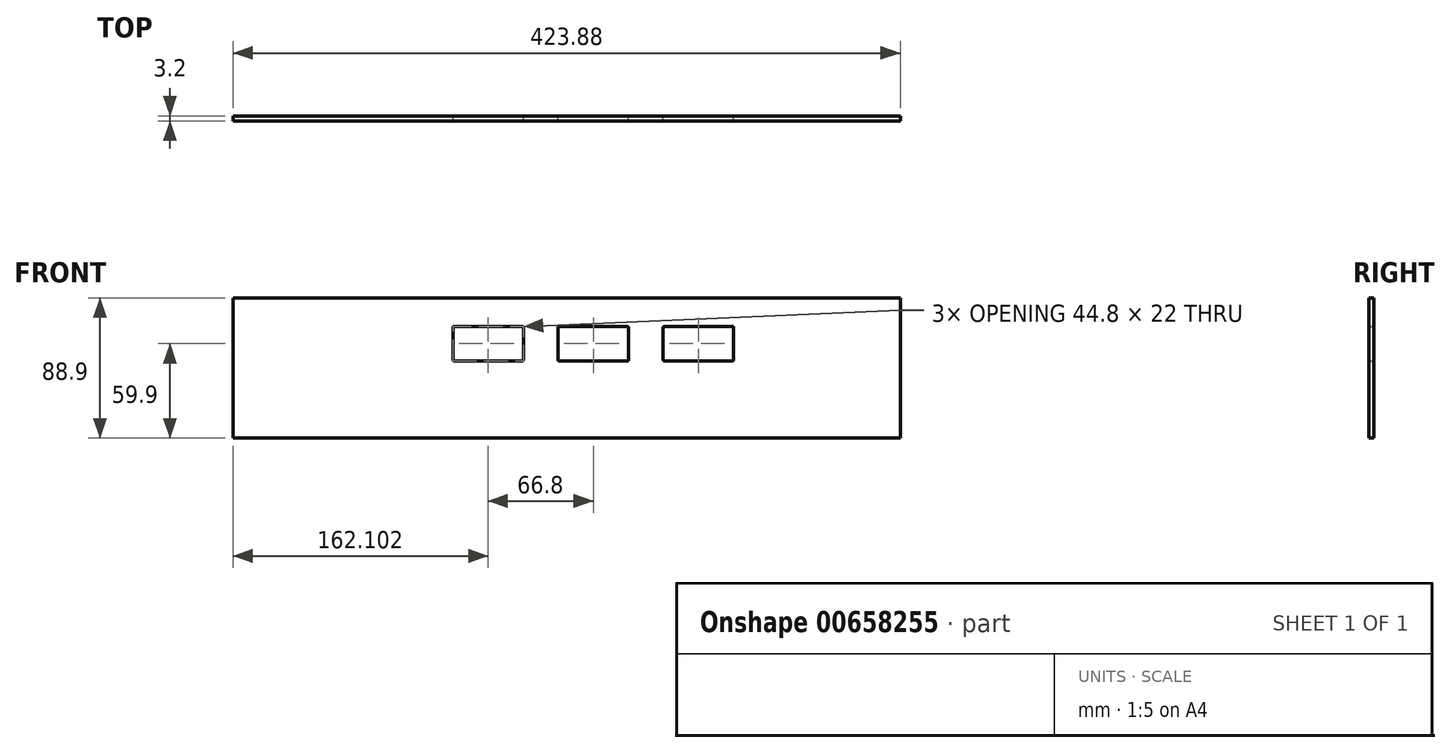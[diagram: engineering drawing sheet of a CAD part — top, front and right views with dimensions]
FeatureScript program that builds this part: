
annotation { "Feature Type Name" : "Feature", "Feature Type Description" : "" }
export const myFeature = defineFeature(function(context is Context, id is Id, definition is map)
    precondition{}
    {
        {
            var Q0;
            Q0=qCreatedBy(makeId("Front.planeOp"),FACE);
            var sketch = newSketch(context, id + "F0", { "sketchPlane" : qUnion([Q0])});
            skLineSegment(sketch, "E0.bottom", {"start": v(-211.94, 44.45) * mm, "end": v(211.94, 44.45) * mm});
            skLineSegment(sketch, "E0.top", {"start": v(-211.94, -44.45) * mm, "end": v(211.94, -44.45) * mm});
            skLineSegment(sketch, "E0.left", {"start": v(-211.94, 44.45) * mm, "end": v(-211.94, -44.45) * mm});
            skLineSegment(sketch, "E0.right", {"start": v(211.94, 44.45) * mm, "end": v(211.94, -44.45) * mm});
            skPoint(sketch, "E1", {"position": v(0, 44.45) * mm});
            skPoint(sketch, "E2", {"position": v(-211.94, 0) * mm});
            skLineSegment(sketch, "E3", {"start": v(-211.94, 34.93) * mm, "end": v(211.94, 34.93) * mm, "construction": true});
            skLineSegment(sketch, "E4", {"start": v(-211.94, -34.93) * mm, "end": v(211.94, -34.93) * mm, "construction": true});
            skLineSegment(sketch, "E5", {"start": v(-211.94, 34.93) * mm, "end": v(-211.94, -34.93) * mm, "construction": true});
            skLineSegment(sketch, "E6", {"start": v(-97.64, 34.93) * mm, "end": v(-97.64, -34.93) * mm, "construction": true});
            skLineSegment(sketch, "E7", {"start": v(-72.24, 34.93) * mm, "end": v(-72.24, -34.93) * mm, "construction": true});
            skLineSegment(sketch, "E8.bottom", {"start": v(-71.44, 26.45) * mm, "end": v(-28.23, 26.45) * mm});
            skLineSegment(sketch, "E8.top", {"start": v(-71.44, 4.45) * mm, "end": v(-28.23, 4.45) * mm});
            skLineSegment(sketch, "E8.left", {"start": v(-72.24, 25.66) * mm, "end": v(-72.24, 5.24) * mm});
            skLineSegment(sketch, "E8.right", {"start": v(-27.44, 25.66) * mm, "end": v(-27.44, 5.24) * mm});
            skLineSegment(sketch, "E9.bottom", {"start": v(-4.64, 26.45) * mm, "end": v(38.57, 26.45) * mm});
            skLineSegment(sketch, "E9.top", {"start": v(-4.64, 4.45) * mm, "end": v(38.57, 4.45) * mm});
            skLineSegment(sketch, "E9.left", {"start": v(-5.44, 25.66) * mm, "end": v(-5.44, 5.24) * mm});
            skLineSegment(sketch, "E9.right", {"start": v(39.36, 25.66) * mm, "end": v(39.36, 5.24) * mm});
            skLineSegment(sketch, "E10.bottom", {"start": v(62.16, 26.45) * mm, "end": v(105.37, 26.45) * mm});
            skLineSegment(sketch, "E10.top", {"start": v(62.16, 4.45) * mm, "end": v(105.37, 4.45) * mm});
            skLineSegment(sketch, "E10.left", {"start": v(61.36, 25.66) * mm, "end": v(61.36, 5.24) * mm});
            skLineSegment(sketch, "E10.right", {"start": v(106.16, 25.66) * mm, "end": v(106.16, 5.24) * mm});
            skPoint(sketch, "E11.visualSharp", {"position": v(-27.44, 26.45) * mm});
            skArc(sketch, "E11.filletArc", {"start": v(-27.44, 25.66) * mm, "mid": v(-27.67, 26.22) * mm, "end": v(-28.23, 26.45) * mm});
            skPoint(sketch, "E12.visualSharp", {"position": v(-27.44, 4.45) * mm});
            skArc(sketch, "E12.filletArc", {"start": v(-28.23, 4.45) * mm, "mid": v(-27.67, 4.68) * mm, "end": v(-27.44, 5.24) * mm});
            skPoint(sketch, "E13.visualSharp", {"position": v(-72.24, 4.45) * mm});
            skArc(sketch, "E13.filletArc", {"start": v(-72.24, 5.24) * mm, "mid": v(-72, 4.68) * mm, "end": v(-71.44, 4.45) * mm});
            skPoint(sketch, "E14.visualSharp", {"position": v(-72.24, 26.45) * mm});
            skArc(sketch, "E14.filletArc", {"start": v(-71.44, 26.45) * mm, "mid": v(-72, 26.22) * mm, "end": v(-72.24, 25.66) * mm});
            skPoint(sketch, "E15.visualSharp", {"position": v(-5.44, 26.45) * mm});
            skArc(sketch, "E15.filletArc", {"start": v(-4.64, 26.45) * mm, "mid": v(-5.2, 26.22) * mm, "end": v(-5.44, 25.66) * mm});
            skPoint(sketch, "E16.visualSharp", {"position": v(-5.44, 4.45) * mm});
            skArc(sketch, "E16.filletArc", {"start": v(-5.44, 5.24) * mm, "mid": v(-5.2, 4.68) * mm, "end": v(-4.64, 4.45) * mm});
            skPoint(sketch, "E17.visualSharp", {"position": v(39.36, 26.45) * mm});
            skArc(sketch, "E17.filletArc", {"start": v(39.36, 25.66) * mm, "mid": v(39.13, 26.22) * mm, "end": v(38.57, 26.45) * mm});
            skPoint(sketch, "E18.visualSharp", {"position": v(39.36, 4.45) * mm});
            skArc(sketch, "E18.filletArc", {"start": v(38.57, 4.45) * mm, "mid": v(39.13, 4.68) * mm, "end": v(39.36, 5.24) * mm});
            skPoint(sketch, "E19.visualSharp", {"position": v(61.36, 26.45) * mm});
            skArc(sketch, "E19.filletArc", {"start": v(62.16, 26.45) * mm, "mid": v(61.6, 26.22) * mm, "end": v(61.36, 25.66) * mm});
            skPoint(sketch, "E20.visualSharp", {"position": v(61.36, 4.45) * mm});
            skArc(sketch, "E20.filletArc", {"start": v(61.36, 5.24) * mm, "mid": v(61.6, 4.68) * mm, "end": v(62.16, 4.45) * mm});
            skPoint(sketch, "E21.visualSharp", {"position": v(106.16, 26.45) * mm});
            skArc(sketch, "E21.filletArc", {"start": v(106.16, 25.66) * mm, "mid": v(105.93, 26.22) * mm, "end": v(105.37, 26.45) * mm});
            skPoint(sketch, "E22.visualSharp", {"position": v(106.16, 4.45) * mm});
            skArc(sketch, "E22.filletArc", {"start": v(105.37, 4.45) * mm, "mid": v(105.93, 4.68) * mm, "end": v(106.16, 5.24) * mm});
            skSolve(sketch);
        }
        {
            var Q0;
            Q0 = qSketchRegion(id + "F0", true);
            extrude(context, id + "F1", {"entities" : qUnion([Q0]), "depth" : 3.2 * mm, "offsetDistance" : 25 * mm});
        }
    });
